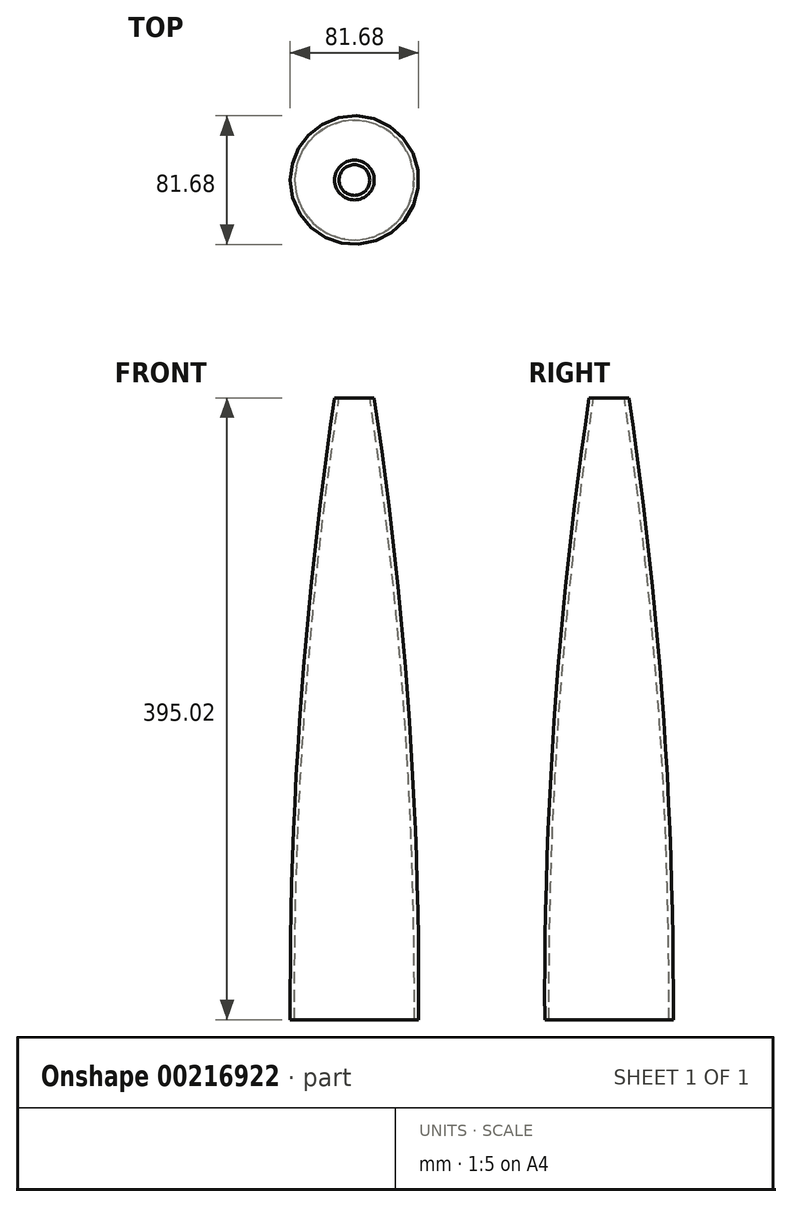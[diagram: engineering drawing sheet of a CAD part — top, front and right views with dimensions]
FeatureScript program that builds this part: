
annotation { "Feature Type Name" : "Feature", "Feature Type Description" : "" }
export const myFeature = defineFeature(function(context is Context, id is Id, definition is map)
    precondition{}
    {
        {
            var Q0;
            Q0=qCreatedBy(makeId("Front.planeOp"),FACE);
            var sketch = newSketch(context, id + "F0", { "sketchPlane" : qUnion([Q0])});
            skLineSegment(sketch, "E0", {"start": v(0, 0) * mm, "end": v(0, 395) * mm, "construction": true});
            skLineSegment(sketch, "E1", {"start": v(0, 395) * mm, "end": v(-9.75, 395) * mm, "construction": true});
            skLineSegment(sketch, "E2", {"start": v(0, 0) * mm, "end": v(-38, 0) * mm, "construction": true});
            skLineSegment(sketch, "E3", {"start": v(0, 352) * mm, "end": v(-15.8, 352) * mm, "construction": true});
            skArc(sketch, "E4", {"start": v(-9.75, 395) * mm, "mid": v(-31.46, 198.04) * mm, "end": v(-38, 0) * mm});
            skArc(sketch, "E5.0", {"start": v(-12.58, 395) * mm, "mid": v(-34.27, 198.03) * mm, "end": v(-40.8, -0.02) * mm});
            skLineSegment(sketch, "E6", {"start": v(-9.75, 395) * mm, "end": v(-12.58, 395) * mm});
            skLineSegment(sketch, "E7", {"start": v(-40.8, -0.02) * mm, "end": v(-38, 0) * mm});
            skLineSegment(sketch, "E8", {"start": v(-26.12, 261.65) * mm, "end": v(0, 261.65) * mm, "construction": true});
            skLineSegment(sketch, "E9", {"start": v(0, 166.4) * mm, "end": v(-33.53, 166.4) * mm, "construction": true});
            skSolve(sketch);
        }
        {
            var Q0;
            Q0 = qSketchRegion(id + "F0", true);
            var Q1;
            Q1=sQuery(id+"F0.wireOp",EDGE,"E0");
            revolve(context, id + "F1", {"entities" : qUnion([Q0]), "axis" : qUnion([Q1]), "revolveType" : RevolveType.FULL});
        }
    });
